# Revit family: Plumbing-Lavatories-Sloan-Valve-SS3017_
name_source: partatom
category: Plumbing Fixtures
units: mm (PartAtom-declared; Revit-internal decimal feet)

## family parameters
Cut with Voids When Loaded = Yes
Host = Face
OmniClass Number = 23.45.05.14.14
OmniClass Title = Sinks/Lavatories
Part Type = Normal
Room Calculation Point = No
Round Connector Dimension = Use Diameter
Shared = No

## types (1)
- SS-3017
    Assembly Code = D2010400
    CW Connection = Yes
    CWFU = 1.5
    Cold Water Connection Diameter = 0"
    Cold Water Connector Description = Cold Water Connector d3/8"
    Default Elevation = 0"
    Depth = 18 1/4"
    Description = Enamelled Cast Iron Wall-Mounted Backsplash Lavatory.
    Edition number = 1
    HW Connection = Yes
    HWFU = 1.5
    Height = 12"
    Hot Water Connection Diameter = 0"
    Hot Water Connector Description = Hot Water Connector d3/8"
    Keynote = 10000
    Manufacturer = Sloan Valve
    Model = SS-3017
    Part Number = 3873017
    Product Material = Sloan Valve - Enamelled Cast Iron - White
    Product data url = https://bimobject.com
    Sanitary Drain Connection Diameter = 1"
    Sanitary Drain Connector Description = Sanitary Drain Connector d1 1/4"
    URL = www.sloanvalve.com
    Valve Pressure Drop = 0.00 psi
    Vent Connection = Yes
    WFU = 2
    Waste Connection = Yes
    Water Flow = 0 GPM
    Width = 20 1/4"

## geometry (parser evidence)
native form markers: Sweep x2
no freeform markers — native parametric forms only
